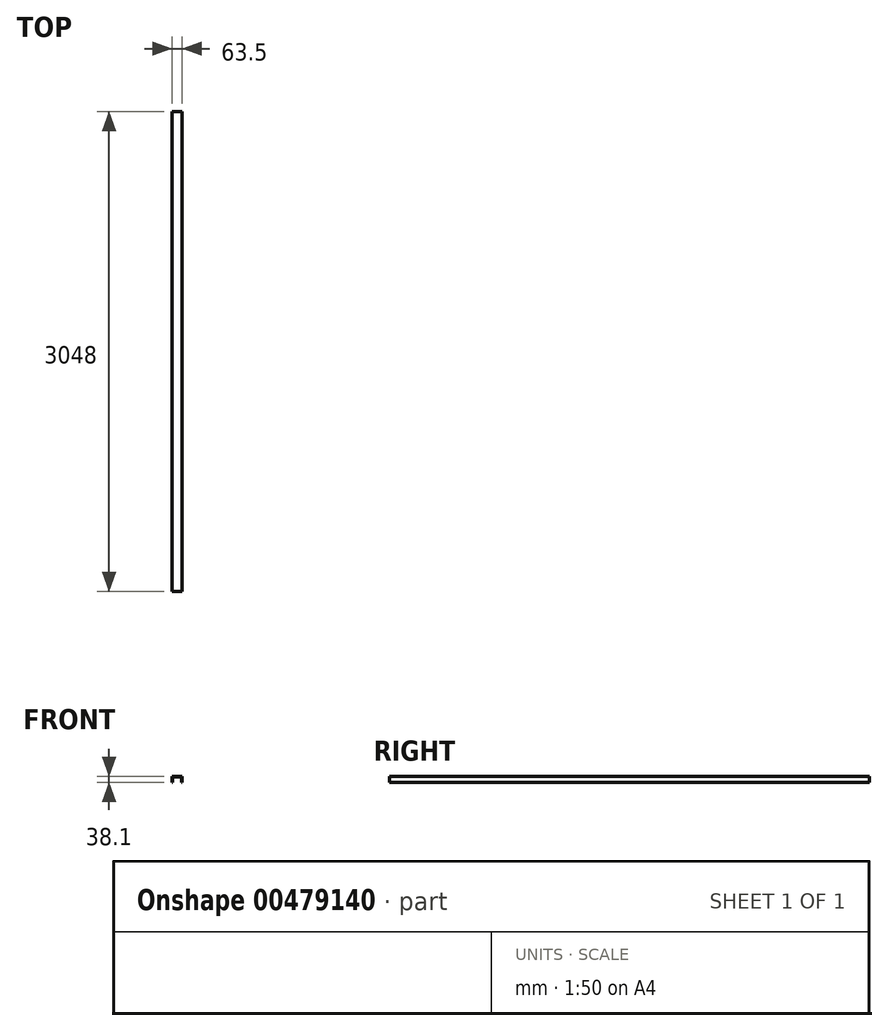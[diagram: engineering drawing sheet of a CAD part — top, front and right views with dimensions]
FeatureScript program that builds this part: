
annotation { "Feature Type Name" : "Feature", "Feature Type Description" : "" }
export const myFeature = defineFeature(function(context is Context, id is Id, definition is map)
    precondition{}
    {
        {
            var Q0;
            Q0=qCreatedBy(makeId("Front.planeOp"),FACE);
            var sketch = newSketch(context, id + "F0", { "sketchPlane" : qUnion([Q0])});
            skLineSegment(sketch, "E0", {"start": v(-31.75, 0) * mm, "end": v(31.75, 0) * mm});
            skLineSegment(sketch, "E1", {"start": v(31.75, 0) * mm, "end": v(31.75, -38.1) * mm});
            skLineSegment(sketch, "E2", {"start": v(31.75, -38.1) * mm, "end": v(28.57, -38.1) * mm});
            skLineSegment(sketch, "E3", {"start": v(28.57, -38.1) * mm, "end": v(28.57, -3.17) * mm});
            skLineSegment(sketch, "E4", {"start": v(28.57, -3.17) * mm, "end": v(-28.57, -3.18) * mm});
            skLineSegment(sketch, "E5", {"start": v(-28.57, -3.18) * mm, "end": v(-28.57, -38.1) * mm});
            skLineSegment(sketch, "E6", {"start": v(-28.57, -38.1) * mm, "end": v(-31.75, -38.1) * mm});
            skLineSegment(sketch, "E7", {"start": v(-31.75, -38.1) * mm, "end": v(-31.75, 0) * mm});
            skSolve(sketch);
        }
        {
            var Q0;
            Q0 = qSketchRegion(id + "F0", true);
            var Q1;
            Q1=makeQuery(id+"F0.imprint","IMPRINT",FACE,{"disambiguationData":[TD([[makeQuery(id+"F0.imprint","IMPRINT",EDGE,{"derivedFrom":sQuery(id+"F0.wireOp",EDGE,"E0")}),-1.0]])]});
            extrude(context, id + "F1", {"entities" : qUnion([Q0, Q1]), "oppositeDirection" : true, "depth" : 3048 * mm});
        }
    });
